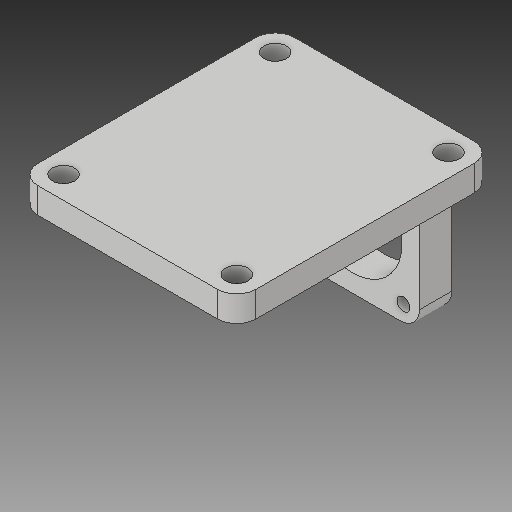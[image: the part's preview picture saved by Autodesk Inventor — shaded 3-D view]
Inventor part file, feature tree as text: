
AUTODESK INVENTOR PART (.ipt)
format: ipt  version: 2019 (Build 230136000, 136)  size: 154,112 bytes
history: native  units: mm
features: other x3, sketch x2
ambient origin geometry x8: Origin, YZ Plane, XZ Plane, XY Plane, X Axis, Y Axis, Z Axis, Center Point
bodies: Solid1 (feature_tree)
feature tree (5):
  other  "Nema8_holder.ipt"
  other  "Solid1::Nema8_holder.ipt"
  other  "TaggingFeature1"
  sketch  "Sketch1"  dims[d0=10.0mm]
  sketch  "Sketch2"
